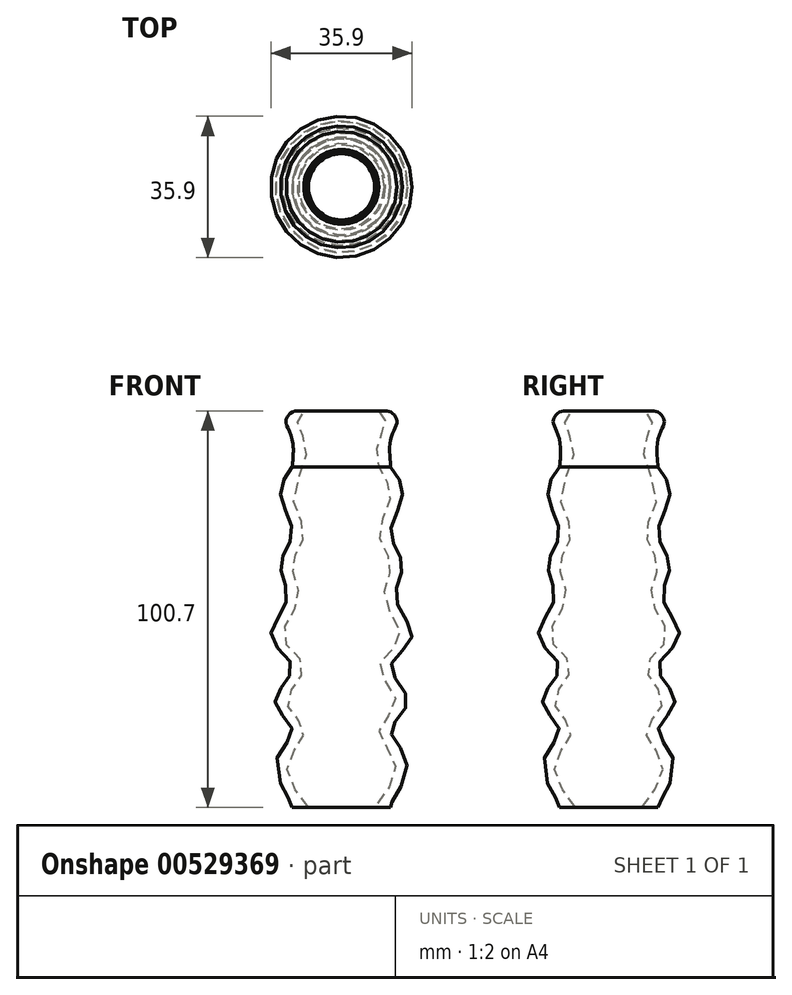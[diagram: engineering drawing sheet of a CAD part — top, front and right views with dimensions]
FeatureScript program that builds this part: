
annotation { "Feature Type Name" : "Feature", "Feature Type Description" : "" }
export const myFeature = defineFeature(function(context is Context, id is Id, definition is map)
    precondition{}
    {
        {
            var Q0;
            Q0=qCreatedBy(makeId("Front.planeOp"),FACE);
            var sketch = newSketch(context, id + "F0", { "sketchPlane" : qUnion([Q0])});
            skLineSegment(sketch, "E0", {"start": v(12.52, -43.09) * mm, "end": v(8.4, -43.09) * mm});
            skFitSpline(sketch, "E1", {"points": [v(12.52, -43.09) * mm, v(12.52, -42.25) * mm, v(16.65, -31.8) * mm, v(12.52, -23.55) * mm, v(16.83, -16.11) * mm, v(12.52, -7.44) * mm, v(17.89, 0) * mm, v(13.83, 9.9) * mm, v(15.5, 18.58) * mm, v(12.52, 26.43) * mm, v(15.5, 36.34) * mm, v(12.52, 43.37) * mm], "startDerivative": vector(0, 86.22) * mm, "endDerivative": vector(-54.46, 71.2) * mm});
            skFitSpline(sketch, "E2", {"points": [v(12.52, 43.37) * mm, v(12.52, 50.4) * mm, v(14.1, 55.03) * mm, v(12.52, 57.3) * mm, v(9.52, 57.53) * mm], "startDerivative": vector(-1.05, 10.59) * mm, "endDerivative": vector(-17.49, -1.06) * mm});
            skFitSpline(sketch, "E3", {"points": [v(9.52, 57.53) * mm, v(11.1, 55.03) * mm, v(9.52, 50.4) * mm, v(9.52, 43.37) * mm, v(12.5, 36.34) * mm, v(9.52, 26.43) * mm, v(12.5, 18.58) * mm, v(10.83, 9.9) * mm, v(14.89, 0) * mm, v(9.52, -7.44) * mm, v(13.83, -16.11) * mm, v(9.52, -23.55) * mm, v(13.65, -31.8) * mm, v(8.4, -43.09) * mm], "startDerivative": vector(49.05, -49.98) * mm, "endDerivative": vector(-96.54, -123.7) * mm});
            skSolve(sketch);
        }
        {
            var Q0;
            Q0=qCreatedBy(makeId("Front.planeOp"),FACE);
            var sketch = newSketch(context, id + "F1", { "sketchPlane" : qUnion([Q0])});
            skLineSegment(sketch, "E4", {"start": v(0, 34.2) * mm, "end": v(0, -20.27) * mm});
            skSolve(sketch);
        }
        {
            var Q0;
            Q0 = qSketchRegion(id + "F0", true);
            var Q1;
            Q1=sQuery(id+"F1.wireOp",EDGE,"E4");
            revolve(context, id + "F2", {"entities" : qUnion([Q0]), "axis" : qUnion([Q1]), "revolveType" : RevolveType.FULL});
        }
    });
